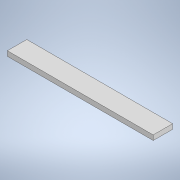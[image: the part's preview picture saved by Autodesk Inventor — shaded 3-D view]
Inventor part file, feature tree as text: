
AUTODESK INVENTOR PART (.ipt)
format: ipt  version: 2020.2 (Build 242310000, 310)  size: 95,744 bytes
history: native  units: mm
features: extrude x1, sketch x1
ambient origin geometry x8: Origin, YZ Plane, XZ Plane, XY Plane, X Axis, Y Axis, Z Axis, Center Point
bodies: Solid1 (feature_tree)
feature tree (2):
  extrude  "Extrusion1"  Depth=100.0mm
  sketch  "Sketch1"  dims[d0=5000.0mm d1=5000.0mm d2=3000.0mm d3=400.0mm d4=1500.0mm d5=100.0mm d6=0.0mm]
